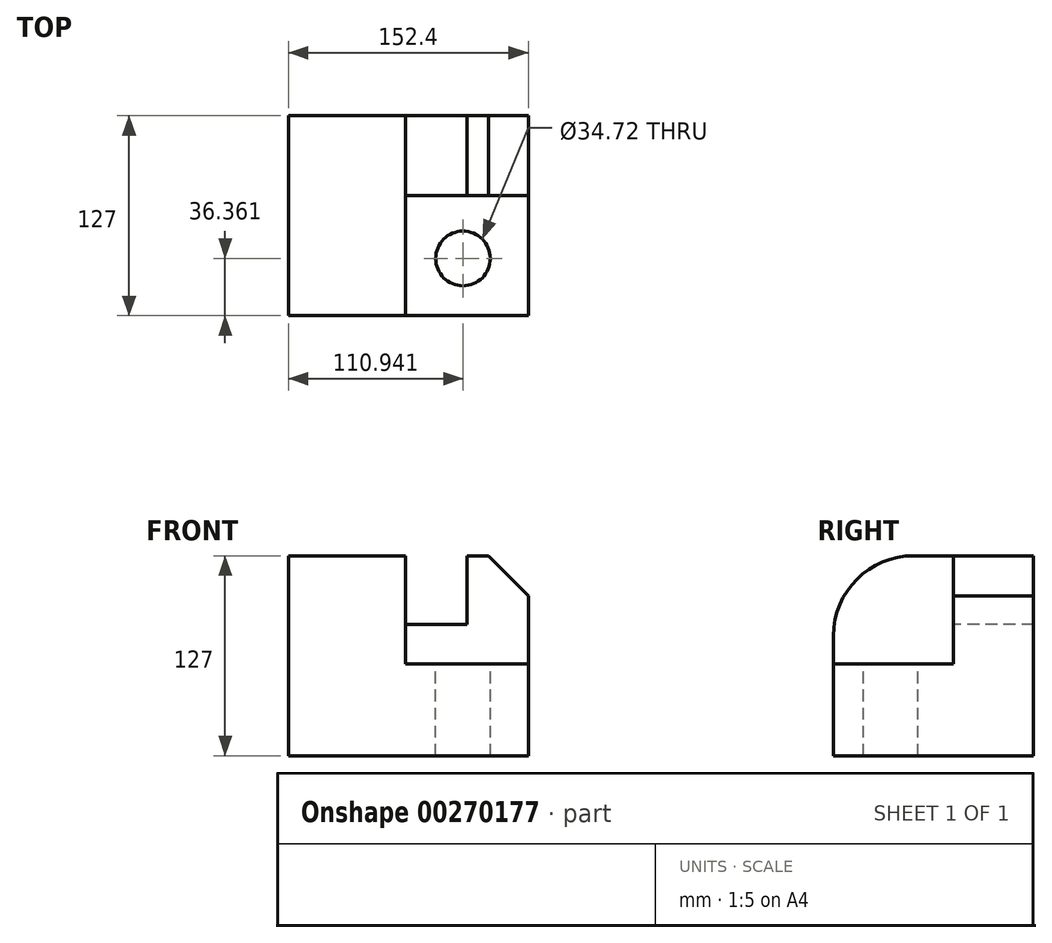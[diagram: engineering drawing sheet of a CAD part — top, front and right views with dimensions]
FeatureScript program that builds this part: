
annotation { "Feature Type Name" : "Feature", "Feature Type Description" : "" }
export const myFeature = defineFeature(function(context is Context, id is Id, definition is map)
    precondition{}
    {
        {
            var Q0;
            Q0=qCreatedBy(makeId("Front.planeOp"),FACE);
            var sketch = newSketch(context, id + "F0", { "sketchPlane" : qUnion([Q0])});
            skLineSegment(sketch, "E0.bottom", {"start": v(-74.46, 68.82) * mm, "end": v(77.94, 68.82) * mm});
            skLineSegment(sketch, "E0.top", {"start": v(-74.46, -58.18) * mm, "end": v(77.94, -58.18) * mm});
            skLineSegment(sketch, "E0.left", {"start": v(-74.46, 68.82) * mm, "end": v(-74.46, -58.18) * mm});
            skLineSegment(sketch, "E0.right", {"start": v(77.94, 68.82) * mm, "end": v(77.94, -58.18) * mm});
            skSolve(sketch);
        }
        {
            var Q0;
            Q0=makeQuery(id+"F0.imprint","IMPRINT",FACE,{"disambiguationData":[TD([[makeQuery(id+"F0.imprint","IMPRINT",EDGE,{"derivedFrom":sQuery(id+"F0.wireOp",EDGE,"E0.bottom")}),-1.0]])]});
            extrude(context, id + "F1", {"entities" : qUnion([Q0]), "depth" : 127 * mm});
        }
        {
            var Q0;
            Q0=makeQuery(id+"F1.opExtrude","CAP_FACE",FACE,{"disambiguationData":[OSD([sQuery(id+"F0.wireOp",EDGE,"E0.bottom"),sQuery(id+"F0.wireOp",EDGE,"E0.top"),sQuery(id+"F0.wireOp",EDGE,"E0.left"),sQuery(id+"F0.wireOp",EDGE,"E0.right")])],"isStart":false});
            var sketch = newSketch(context, id + "F2", { "sketchPlane" : qUnion([Q0])});
            skLineSegment(sketch, "E1", {"start": v(0, 68.82) * mm, "end": v(0, 0) * mm});
            skPoint(sketch, "E1.startSnap0", {"position": v(1.74, 68.82) * mm});
            skLineSegment(sketch, "E2", {"start": v(0, 0) * mm, "end": v(77.94, 0) * mm});
            skLineSegment(sketch, "E3", {"start": v(77.94, 0) * mm, "end": v(77.94, 68.82) * mm});
            skLineSegment(sketch, "E4", {"start": v(77.94, 68.82) * mm, "end": v(1.74, 68.82) * mm});
            skSolve(sketch);
        }
        {
            var Q0;
            {var subQ1=sQuery(id+"F2.wireOp",EDGE,"E1");Q0=makeQuery(id+"F2.imprint","IMPRINT",FACE,{"disambiguationData":[TD([[makeQuery(id+"F2.imprint","IMPRINT",EDGE,{"derivedFrom":subQ1}),1.0]])]});}
            extrude(context, id + "F3", {"entities" : qUnion([Q0]), "operationType" : NewBodyOperationType.REMOVE, "oppositeDirection" : true, "depth" : 76.2 * mm});
        }
        {
            var Q0;
            Q0=makeQuery(id+"F3.boolean.opBoolean","COPY",FACE,{"derivedFrom":makeQuery(id+"F3.opExtrude","CAP_FACE",FACE,{"disambiguationData":[OSD([sQuery(id+"F0.wireOp",EDGE,"E0.bottom"),sQuery(id+"F2.wireOp",EDGE,"E1"),sQuery(id+"F2.wireOp",EDGE,"E2"),sQuery(id+"F2.wireOp",EDGE,"E3"),sQuery(id+"F2.wireOp",EDGE,"E4")])],"isStart":false})});
            var sketch = newSketch(context, id + "F4", { "sketchPlane" : qUnion([Q0])});
            skLineSegment(sketch, "E5", {"start": v(38.97, 68.82) * mm, "end": v(38.97, 25.26) * mm});
            skLineSegment(sketch, "E6", {"start": v(38.97, 25.26) * mm, "end": v(0, 25.26) * mm});
            skLineSegment(sketch, "E7", {"start": v(0, 25.26) * mm, "end": v(0, 68.82) * mm});
            skLineSegment(sketch, "E8", {"start": v(0, 68.82) * mm, "end": v(38.97, 68.82) * mm});
            skSolve(sketch);
        }
        {
            var Q0;
            Q0=makeQuery(id+"F4.imprint","IMPRINT",FACE,{"disambiguationData":[TD([[makeQuery(id+"F4.imprint","IMPRINT",EDGE,{"derivedFrom":sQuery(id+"F4.wireOp",EDGE,"E5")}),-1.0]])]});
            extrude(context, id + "F5", {"entities" : qUnion([Q0]), "operationType" : NewBodyOperationType.REMOVE, "endBound" : BoundingType.THROUGH_ALL, "oppositeDirection" : true, "depth" : 25.4 * mm});
        }
        {
            var Q0;
            Q0=makeQuery(id+"F3.boolean.opBoolean","COPY",FACE,{"derivedFrom":makeQuery(id+"F3.opExtrude","SWEPT_FACE",FACE,{"disambiguationData":[OSD([sQuery(id+"F2.wireOp",EDGE,"E2")])]})});
            var sketch = newSketch(context, id + "F6", { "sketchPlane" : qUnion([Q0])});
            skCircle(sketch, "E9", {"center": v(36.48, -90.64) * mm, "radius": 17.36 * mm});
            skSolve(sketch);
        }
        {
            var Q0;
            Q0=makeQuery(id+"F6.imprint","IMPRINT",FACE,{"disambiguationData":[TD([[makeQuery(id+"F6.imprint","IMPRINT",EDGE,{"derivedFrom":sQuery(id+"F6.wireOp",EDGE,"E9")}),1.0]])]});
            extrude(context, id + "F7", {"entities" : qUnion([Q0]), "operationType" : NewBodyOperationType.REMOVE, "endBound" : BoundingType.THROUGH_ALL, "oppositeDirection" : true, "depth" : 25.4 * mm});
        }
        {
            var Q0;
            Q0=makeQuery(id+"F1.opExtrude","SWEPT_EDGE",EDGE,{"disambiguationData":[OSD([sQuery(id+"F0.wireOp",EDGE,"E0.bottom"),sQuery(id+"F0.wireOp",EDGE,"E0.right")])]});
            chamfer(context, id + "F8", {"entities" : qUnion([Q0]), "width" : 25.4 * mm, "tangentPropagation" : true});
        }
        {
            var Q0;
            Q0=makeQuery(id+"F1.opExtrude","CAP_EDGE",EDGE,{"disambiguationData":[OSD([sQuery(id+"F0.wireOp",EDGE,"E0.bottom")])],"isStart":false});
            fillet(context, id + "F9", {"entities" : qUnion([Q0]), "radius" : 50.8 * mm, "tangentPropagation" : true, "allowEdgeOverflow" : false});
        }
    });
